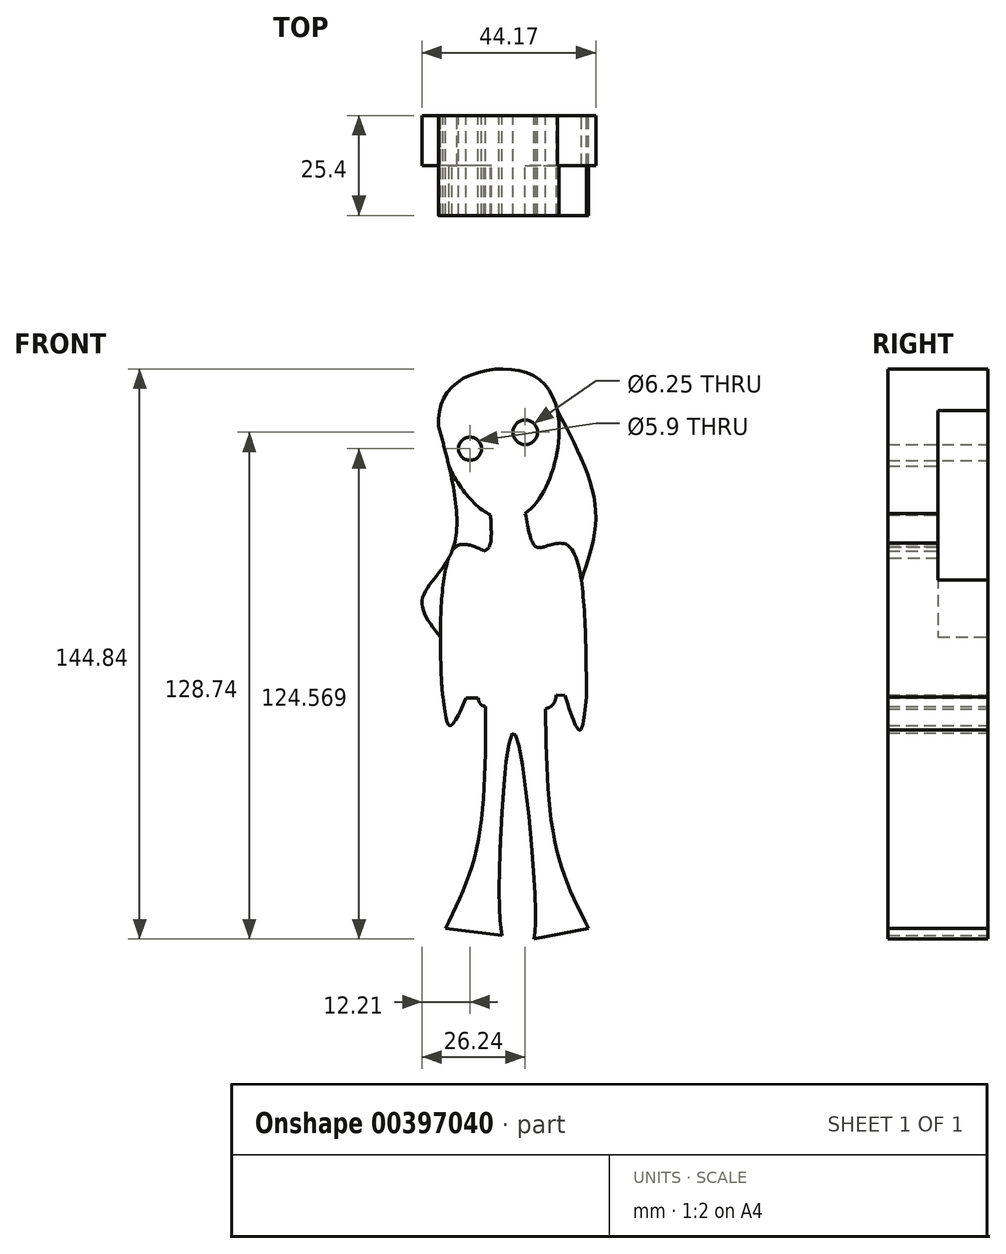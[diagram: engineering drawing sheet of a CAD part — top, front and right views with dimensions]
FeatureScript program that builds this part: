
annotation { "Feature Type Name" : "Feature", "Feature Type Description" : "" }
export const myFeature = defineFeature(function(context is Context, id is Id, definition is map)
    precondition{}
    {
        {
            var Q0;
            Q0=qCreatedBy(makeId("Front.planeOp"),FACE);
            var sketch = newSketch(context, id + "F0", { "sketchPlane" : qUnion([Q0])});
            skFitSpline(sketch, "E0", {"points": [v(-4.36, 34.32) * mm, v(-18.4, 45.88) * mm, v(-18.96, 67.69) * mm, v(3.8, 69.77) * mm, v(6.64, 45.88) * mm, v(-4.36, 34.32) * mm]});
            skFitSpline(sketch, "E1", {"points": [v(-8.82, 35.45) * mm, v(-9.1, 27.5) * mm, v(-10.43, 26.35) * mm], "startDerivative": vector(0.9, -14.4) * mm, "endDerivative": vector(-4.76, -2.27) * mm});
            skFitSpline(sketch, "E2", {"points": [v(0, 35.9) * mm, v(2.65, 27.5) * mm, v(5.12, 27.5) * mm], "startDerivative": vector(3.05, -17.06) * mm, "endDerivative": vector(7.66, 2.22) * mm});
            skFitSpline(sketch, "E3", {"points": [v(-9.92, 26.6) * mm, v(0, 25.22) * mm, v(4.24, 27.24) * mm], "startDerivative": vector(18.58, -4.49) * mm, "endDerivative": vector(9.15, 6.45) * mm});
            skFitSpline(sketch, "E4", {"points": [v(-10.43, 26.35) * mm, v(-18.58, 26.35) * mm, v(-21.05, -9.86) * mm, v(-20.86, -10.8) * mm], "startDerivative": vector(-32.22, 15.19) * mm, "endDerivative": vector(1.72, -3.77) * mm});
            skFitSpline(sketch, "E5", {"points": [v(5.12, 27.5) * mm, v(11.19, 27.5) * mm, v(15.55, -10.8) * mm], "startDerivative": vector(23.53, 7.6) * mm, "endDerivative": vector(0.62, -72.64) * mm});
            skFitSpline(sketch, "E6", {"points": [v(-11.97, 14.95) * mm, v(-11.97, -11.06) * mm, v(-10.1, -13.2) * mm, v(5.12, -13.74) * mm, v(7.87, -10.26) * mm, v(7.34, 16.29) * mm], "startDerivative": vector(-3.44, -117.1) * mm, "endDerivative": vector(-6.53, 113.39) * mm});
            skFitSpline(sketch, "E7", {"points": [v(15.55, -10.8) * mm, v(13.84, -19.15) * mm, v(10.05, -10.26) * mm], "startDerivative": vector(-2.6, -25.57) * mm, "endDerivative": vector(-8.34, 26.12) * mm});
            skLineSegment(sketch, "E8", {"start": v(7.87, -10.26) * mm, "end": v(15.55, -10.8) * mm});
            skFitSpline(sketch, "E9", {"points": [v(-20.86, -10.8) * mm, v(-19.15, -18.01) * mm, v(-14.98, -10.8) * mm], "startDerivative": vector(2.4, -21.84) * mm, "endDerivative": vector(9.29, 21.42) * mm});
            skLineSegment(sketch, "E10", {"start": v(-20.86, -10.8) * mm, "end": v(-11.97, -11.06) * mm});
            skFitSpline(sketch, "E11", {"points": [v(-10.1, -13.2) * mm, v(-12.32, -49.1) * mm, v(-20.29, -69.58) * mm], "startDerivative": vector(0, -68.8) * mm, "endDerivative": vector(-21.26, -42.89) * mm});
            skFitSpline(sketch, "E12", {"points": [v(5.12, -13.74) * mm, v(7.87, -49.1) * mm, v(16.12, -69.58) * mm], "startDerivative": vector(1.08, -67.96) * mm, "endDerivative": vector(21.72, -42.72) * mm});
            skFitSpline(sketch, "E13", {"points": [v(-5.88, -71.29) * mm, v(-6.64, -60.86) * mm, v(-3.03, -19.9) * mm, v(2.46, -60.86) * mm, v(2.28, -72.24) * mm], "startDerivative": vector(-6.84, 37.99) * mm, "endDerivative": vector(-4.47, -40.71) * mm});
            skLineSegment(sketch, "E14", {"start": v(-20.29, -69.58) * mm, "end": v(-5.88, -71.29) * mm});
            skLineSegment(sketch, "E15", {"start": v(2.28, -72.24) * mm, "end": v(16.12, -69.58) * mm});
            skFitSpline(sketch, "E16", {"points": [v(-22.02, 58.03) * mm, v(-18.58, 26.35) * mm, v(-26.16, 14.03) * mm, v(-21.55, 4.52) * mm], "startDerivative": vector(21.87, -80.44) * mm, "endDerivative": vector(30.12, -37.67) * mm});
            skCircle(sketch, "E17", {"center": v(-14.03, 52.33) * mm, "radius": 2.95 * mm});
            skCircle(sketch, "E18", {"center": v(0, 56.5) * mm, "radius": 3.13 * mm});
            skFitSpline(sketch, "E19", {"points": [v(8.16, 61.96) * mm, v(17.82, 37.48) * mm, v(14.22, 18.97) * mm], "startDerivative": vector(24.8, -46.52) * mm, "endDerivative": vector(-13.79, -39.28) * mm});
            skSolve(sketch);
        }
        {
            var Q0;
            Q0=makeQuery(id+"F0.imprint","IMPRINT",FACE,{"disambiguationData":[TD([[makeQuery(id+"F0.imprint","IMPRINT",EDGE,{"derivedFrom":sQuery(id+"F0.wireOp",EDGE,"E17")}),-1.0]])]});
            var Q1;
            {var subQ17=sQuery(id+"F0.wireOp",EDGE,"E1");Q1=makeQuery(id+"F0.imprint","IMPRINT",FACE,{"disambiguationData":[TD([[makeQuery(id+"F0.imprint","IMPRINT",EDGE,{"derivedFrom":subQ17}),1.0]])]});}
            var Q2;
            {var subQ1=sQuery(id+"F0.wireOp",EDGE,"E11");Q2=makeQuery(id+"F0.imprint","IMPRINT",FACE,{"disambiguationData":[TD([[makeQuery(id+"F0.imprint","IMPRINT",EDGE,{"derivedFrom":subQ1}),1.0]])]});}
            var Q3;
            {var subQ0=sQuery(id+"F0.wireOp",EDGE,"E8");var subQ1=sQuery(id+"F0.wireOp",EDGE,"E7");var subQ3=makeQuery(id+"F0.imprint","INTERSECT",VERTEX,{"derivedFrom":[subQ1,subQ0]});Q3=makeQuery(id+"F0.imprint","IMPRINT",FACE,{"disambiguationData":[TD([[makeQuery(id+"F0.imprint","IMPRINT",EDGE,{"disambiguationData":[TD([[subQ3,1.0]])],"derivedFrom":subQ1}),-1.0]])]});}
            var Q4;
            {var subQ0=sQuery(id+"F0.wireOp",EDGE,"E10");var subQ1=sQuery(id+"F0.wireOp",EDGE,"E9");var subQ3=makeQuery(id+"F0.imprint","INTERSECT",VERTEX,{"derivedFrom":[subQ1,subQ0]});Q4=makeQuery(id+"F0.imprint","IMPRINT",FACE,{"disambiguationData":[TD([[makeQuery(id+"F0.imprint","IMPRINT",EDGE,{"disambiguationData":[TD([[subQ3,1.0]])],"derivedFrom":subQ1}),1.0]])]});}
            extrude(context, id + "F1", {"entities" : qUnion([Q0, Q1, Q2, Q3, Q4]), "depth" : 25.4 * mm});
        }
        {
            var Q0;
            {var subQ0=sQuery(id+"F0.wireOp",EDGE,"E1");Q0=makeQuery(id+"F0.imprint","IMPRINT",FACE,{"disambiguationData":[TD([[makeQuery(id+"F0.imprint","IMPRINT",EDGE,{"derivedFrom":subQ0}),-1.0]])]});}
            var Q1;
            {var subQ0=sQuery(id+"F0.wireOp",EDGE,"E16");var subQ1=sQuery(id+"F0.wireOp",EDGE,"E4");var subQ2=makeQuery(id+"F0.imprint","INTERSECT",VERTEX,{"disambiguationData":[OD(0.0)],"derivedFrom":[subQ1,subQ0]});Q1=makeQuery(id+"F0.imprint","IMPRINT",FACE,{"disambiguationData":[TD([[makeQuery(id+"F0.imprint","IMPRINT",EDGE,{"disambiguationData":[TD([[subQ2,1.0]])],"derivedFrom":subQ1}),-1.0]])]});}
            var Q2;
            {var subQ0=sQuery(id+"F0.wireOp",EDGE,"E2");Q2=makeQuery(id+"F0.imprint","IMPRINT",FACE,{"disambiguationData":[TD([[makeQuery(id+"F0.imprint","IMPRINT",EDGE,{"derivedFrom":subQ0}),1.0]])]});}
            extrude(context, id + "F2", {"entities" : qUnion([Q0, Q1, Q2]), "operationType" : NewBodyOperationType.ADD, "depth" : 12.7 * mm});
        }
    });
